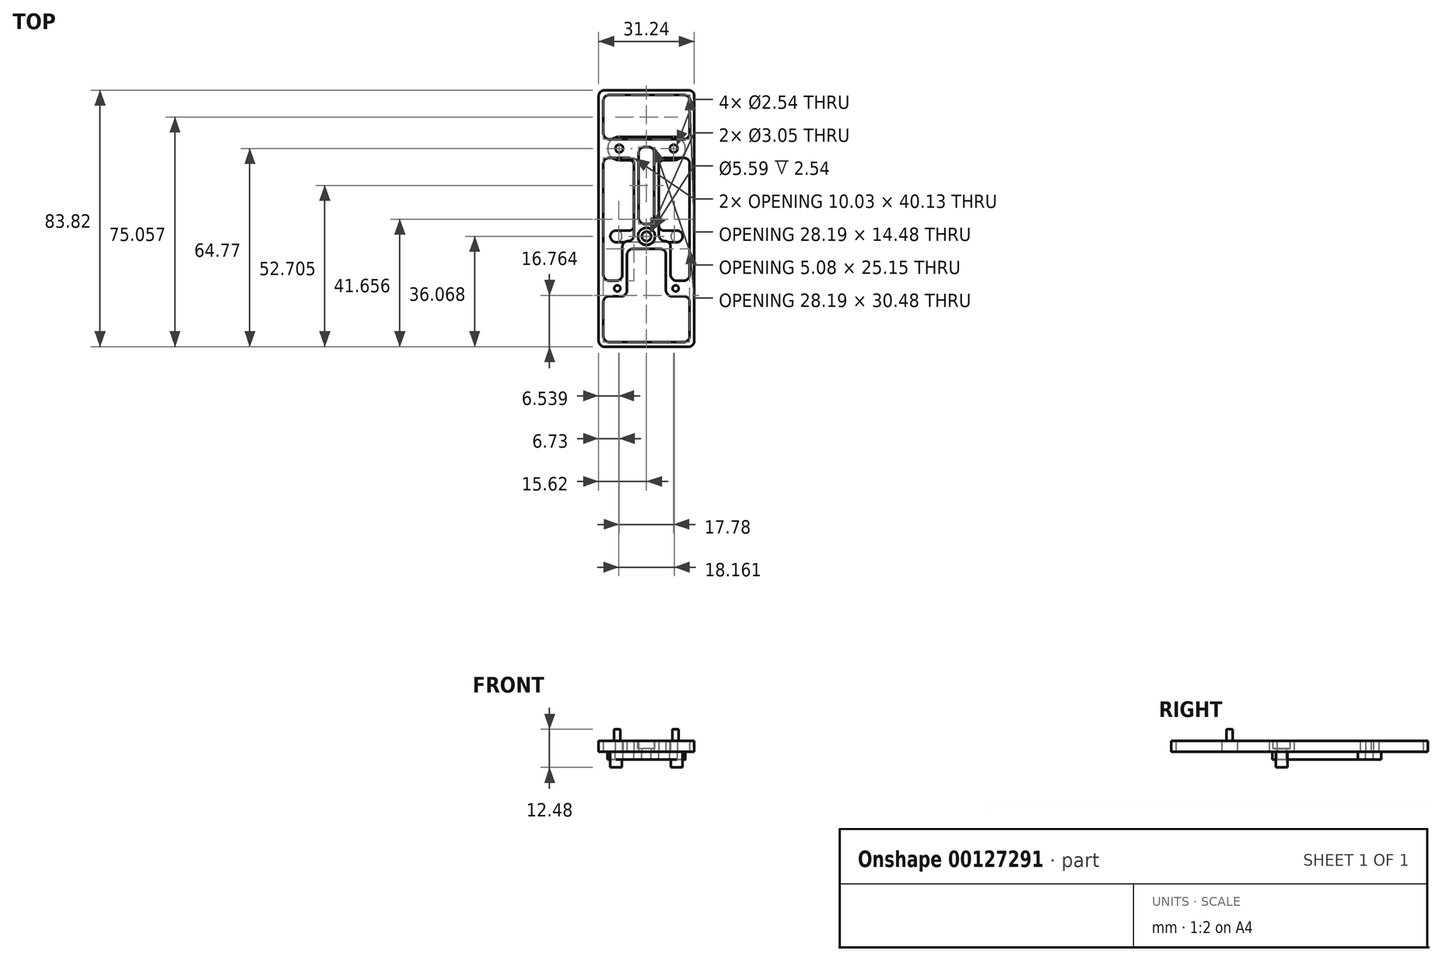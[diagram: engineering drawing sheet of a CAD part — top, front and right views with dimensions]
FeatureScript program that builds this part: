
annotation { "Feature Type Name" : "Feature", "Feature Type Description" : "" }
export const myFeature = defineFeature(function(context is Context, id is Id, definition is map)
    precondition{}
    {
        {
            var Q0;
            Q0=qCreatedBy(makeId("Top.planeOp"),FACE);
            var sketch = newSketch(context, id + "F0", { "sketchPlane" : qUnion([Q0])});
            skLineSegment(sketch, "E0.bottom", {"start": v(-15.62, 41.91) * mm, "end": v(15.62, 41.9) * mm});
            skLineSegment(sketch, "E0.top", {"start": v(-15.62, -41.91) * mm, "end": v(15.62, -41.91) * mm});
            skLineSegment(sketch, "E0.left", {"start": v(-15.62, 41.91) * mm, "end": v(-15.62, -41.91) * mm});
            skLineSegment(sketch, "E0.right", {"start": v(15.62, 41.91) * mm, "end": v(15.62, -41.91) * mm});
            skPoint(sketch, "E1", {"position": v(-15.62, 0) * mm});
            skPoint(sketch, "E2", {"position": v(0, 41.91) * mm});
            skLineSegment(sketch, "E3.bottom", {"start": v(-14.1, 40.39) * mm, "end": v(14.1, 40.39) * mm});
            skLineSegment(sketch, "E3.top", {"start": v(-14.1, -40.39) * mm, "end": v(14.1, -40.39) * mm});
            skLineSegment(sketch, "E3.left", {"start": v(-14.1, 40.39) * mm, "end": v(-14.1, 25.9) * mm});
            skLineSegment(sketch, "E3.right", {"start": v(14.1, 40.39) * mm, "end": v(14.1, 25.9) * mm});
            skPoint(sketch, "E4", {"position": v(0, 40.39) * mm});
            skPoint(sketch, "E5", {"position": v(-14.1, 0) * mm});
            skCircle(sketch, "E6", {"center": v(-8.9, 22.86) * mm, "radius": 1.27 * mm});
            skCircle(sketch, "E7", {"center": v(8.9, 22.86) * mm, "radius": 1.27 * mm});
            skCircle(sketch, "E8", {"center": v(9.53, -22.86) * mm, "radius": 1.02 * mm, "construction": true});
            skCircle(sketch, "E9", {"center": v(-9.53, -22.86) * mm, "radius": 1.02 * mm, "construction": true});
            skLineSegment(sketch, "E10", {"start": v(-8.9, 22.86) * mm, "end": v(-8.9, 19.81) * mm, "construction": true});
            skLineSegment(sketch, "E11", {"start": v(-9.53, -22.86) * mm, "end": v(9.53, -22.86) * mm, "construction": true});
            skLineSegment(sketch, "E12", {"start": v(-8.9, 22.86) * mm, "end": v(8.9, 22.86) * mm, "construction": true});
            skPoint(sketch, "E13", {"position": v(0, 22.86) * mm});
            skLineSegment(sketch, "E14", {"start": v(-14.1, 25.9) * mm, "end": v(-14.1, 19.81) * mm, "construction": true});
            skLineSegment(sketch, "E15", {"start": v(-14.1, 19.81) * mm, "end": v(-14.1, -20.32) * mm});
            skLineSegment(sketch, "E16", {"start": v(14.1, 25.9) * mm, "end": v(14.1, 19.81) * mm, "construction": true});
            skLineSegment(sketch, "E17", {"start": v(14.1, 19.81) * mm, "end": v(14.1, -20.32) * mm});
            skLineSegment(sketch, "E18", {"start": v(-14.1, 25.9) * mm, "end": v(14.1, 25.9) * mm});
            skLineSegment(sketch, "E19", {"start": v(-14.1, 19.81) * mm, "end": v(-4.06, 19.81) * mm});
            skLineSegment(sketch, "E20", {"start": v(-8.9, 22.86) * mm, "end": v(-8.9, 25.9) * mm, "construction": true});
            skCircle(sketch, "E21", {"center": v(0, -5.84) * mm, "radius": 1.52 * mm});
            skLineSegment(sketch, "E22", {"start": v(-4.06, 19.81) * mm, "end": v(-4.06, -7.37) * mm});
            skLineSegment(sketch, "E23", {"start": v(4.06, 19.81) * mm, "end": v(4.06, -7.37) * mm});
            skLineSegment(sketch, "E24", {"start": v(4.06, -7.37) * mm, "end": v(7.87, -7.37) * mm});
            skLineSegment(sketch, "E25", {"start": v(7.87, -7.37) * mm, "end": v(7.87, -20.32) * mm});
            skLineSegment(sketch, "E26", {"start": v(7.87, -20.32) * mm, "end": v(14.1, -20.32) * mm});
            skLineSegment(sketch, "E27", {"start": v(-4.06, -7.37) * mm, "end": v(-7.87, -7.37) * mm});
            skLineSegment(sketch, "E28", {"start": v(-7.87, -7.37) * mm, "end": v(-7.87, -20.32) * mm});
            skLineSegment(sketch, "E29", {"start": v(-7.87, -20.32) * mm, "end": v(-14.1, -20.32) * mm});
            skLineSegment(sketch, "E30", {"start": v(-4.06, -7.37) * mm, "end": v(4.06, -7.37) * mm, "construction": true});
            skPoint(sketch, "E31", {"position": v(0, -7.37) * mm});
            skLineSegment(sketch, "E32", {"start": v(-14.1, -25.4) * mm, "end": v(-6.35, -25.4) * mm});
            skLineSegment(sketch, "E33", {"start": v(-6.35, -25.4) * mm, "end": v(-6.35, -9.9) * mm});
            skLineSegment(sketch, "E34", {"start": v(-6.35, -9.9) * mm, "end": v(6.35, -9.9) * mm});
            skLineSegment(sketch, "E35", {"start": v(6.35, -9.9) * mm, "end": v(6.35, -25.4) * mm});
            skLineSegment(sketch, "E36", {"start": v(6.35, -25.4) * mm, "end": v(14.1, -25.4) * mm});
            skLineSegment(sketch, "E37", {"start": v(-14.1, -20.32) * mm, "end": v(-14.1, -25.4) * mm, "construction": true});
            skLineSegment(sketch, "E38", {"start": v(-14.1, -25.4) * mm, "end": v(-14.1, -40.39) * mm});
            skLineSegment(sketch, "E39", {"start": v(14.1, -25.4) * mm, "end": v(14.1, -40.39) * mm});
            skLineSegment(sketch, "E40", {"start": v(14.1, -20.32) * mm, "end": v(14.1, -25.4) * mm, "construction": true});
            skPoint(sketch, "E41", {"position": v(0, -9.9) * mm});
            skLineSegment(sketch, "E42", {"start": v(-4.06, 19.81) * mm, "end": v(4.06, 19.81) * mm, "construction": true});
            skLineSegment(sketch, "E43", {"start": v(4.06, 19.81) * mm, "end": v(14.1, 19.81) * mm});
            skLineSegment(sketch, "E44", {"start": v(-1.52, -5.84) * mm, "end": v(-4.06, -5.84) * mm, "construction": true});
            skLineSegment(sketch, "E45", {"start": v(-6.35, -9.9) * mm, "end": v(-6.35, -7.37) * mm, "construction": true});
            skPoint(sketch, "E46", {"position": v(-14.1, -22.86) * mm});
            skLineSegment(sketch, "E47", {"start": v(-9.53, -20.32) * mm, "end": v(-9.53, -22.86) * mm, "construction": true});
            skLineSegment(sketch, "E48", {"start": v(-9.53, -22.86) * mm, "end": v(-9.53, -25.4) * mm, "construction": true});
            skLineSegment(sketch, "E49.bottom", {"start": v(-2.54, 23.37) * mm, "end": v(2.54, 23.37) * mm});
            skLineSegment(sketch, "E49.top", {"start": v(-2.54, -1.78) * mm, "end": v(2.54, -1.78) * mm});
            skLineSegment(sketch, "E49.left", {"start": v(-2.54, 23.37) * mm, "end": v(-2.54, -1.78) * mm});
            skLineSegment(sketch, "E49.right", {"start": v(2.54, 23.37) * mm, "end": v(2.54, -1.78) * mm});
            skPoint(sketch, "E50", {"position": v(0, 23.37) * mm});
            skLineSegment(sketch, "E51", {"start": v(0, 23.37) * mm, "end": v(0, 25.9) * mm, "construction": true});
            skLineSegment(sketch, "E52", {"start": v(0, -1.78) * mm, "end": v(0, -4.32) * mm, "construction": true});
            skPoint(sketch, "E53", {"position": v(0, -22.86) * mm});
            skLineSegment(sketch, "E54", {"start": v(0, 22.86) * mm, "end": v(0, -22.86) * mm, "construction": true});
            skPoint(sketch, "E55", {"position": v(0, 0) * mm});
            skSolve(sketch);
        }
        {
            var Q0;
            Q0 = qSketchRegion(id + "F0", true);
            extrude(context, id + "F1", {"entities" : qUnion([Q0]), "depth" : 3.56 * mm});
        }
        {
            var Q0;
            Q0=makeQuery(id+"F1.opExtrude","SWEPT_EDGE",EDGE,{"disambiguationData":[OSD([sQuery(id+"F0.wireOp",EDGE,"E3.bottom"),sQuery(id+"F0.wireOp",EDGE,"E3.right")])]});
            var Q1;
            Q1=makeQuery(id+"F1.opExtrude","SWEPT_EDGE",EDGE,{"disambiguationData":[OSD([sQuery(id+"F0.wireOp",EDGE,"E3.bottom"),sQuery(id+"F0.wireOp",EDGE,"E3.left")])]});
            var Q2;
            Q2=makeQuery(id+"F1.opExtrude","SWEPT_EDGE",EDGE,{"disambiguationData":[OSD([sQuery(id+"F0.wireOp",EDGE,"E3.left"),sQuery(id+"F0.wireOp",EDGE,"E18")])]});
            var Q3;
            Q3=makeQuery(id+"F1.opExtrude","SWEPT_EDGE",EDGE,{"disambiguationData":[OSD([sQuery(id+"F0.wireOp",EDGE,"E3.right"),sQuery(id+"F0.wireOp",EDGE,"E18")])]});
            var Q4;
            Q4=makeQuery(id+"F1.opExtrude","SWEPT_EDGE",EDGE,{"disambiguationData":[OSD([sQuery(id+"F0.wireOp",EDGE,"E0.bottom"),sQuery(id+"F0.wireOp",EDGE,"E0.left")])]});
            var Q5;
            Q5=makeQuery(id+"F1.opExtrude","SWEPT_EDGE",EDGE,{"disambiguationData":[OSD([sQuery(id+"F0.wireOp",EDGE,"E0.bottom"),sQuery(id+"F0.wireOp",EDGE,"E0.right")])]});
            var Q6;
            Q6=makeQuery(id+"F1.opExtrude","SWEPT_EDGE",EDGE,{"disambiguationData":[OSD([sQuery(id+"F0.wireOp",EDGE,"E49.bottom"),sQuery(id+"F0.wireOp",EDGE,"E49.left")])]});
            var Q7;
            Q7=makeQuery(id+"F1.opExtrude","SWEPT_EDGE",EDGE,{"disambiguationData":[OSD([sQuery(id+"F0.wireOp",EDGE,"E15"),sQuery(id+"F0.wireOp",EDGE,"E19")])]});
            var Q8;
            Q8=makeQuery(id+"F1.opExtrude","SWEPT_EDGE",EDGE,{"disambiguationData":[OSD([sQuery(id+"F0.wireOp",EDGE,"E23"),sQuery(id+"F0.wireOp",EDGE,"E43")])]});
            var Q9;
            Q9=makeQuery(id+"F1.opExtrude","SWEPT_EDGE",EDGE,{"disambiguationData":[OSD([sQuery(id+"F0.wireOp",EDGE,"E19"),sQuery(id+"F0.wireOp",EDGE,"E22")])]});
            var Q10;
            Q10=makeQuery(id+"F1.opExtrude","SWEPT_EDGE",EDGE,{"disambiguationData":[OSD([sQuery(id+"F0.wireOp",EDGE,"E49.bottom"),sQuery(id+"F0.wireOp",EDGE,"E49.right")])]});
            var Q11;
            Q11=makeQuery(id+"F1.opExtrude","SWEPT_EDGE",EDGE,{"disambiguationData":[OSD([sQuery(id+"F0.wireOp",EDGE,"E17"),sQuery(id+"F0.wireOp",EDGE,"E43")])]});
            var Q12;
            Q12=makeQuery(id+"F1.opExtrude","SWEPT_EDGE",EDGE,{"disambiguationData":[OSD([sQuery(id+"F0.wireOp",EDGE,"E28"),sQuery(id+"F0.wireOp",EDGE,"E29")])]});
            var Q13;
            Q13=makeQuery(id+"F1.opExtrude","SWEPT_EDGE",EDGE,{"disambiguationData":[OSD([sQuery(id+"F0.wireOp",EDGE,"E27"),sQuery(id+"F0.wireOp",EDGE,"E28")])]});
            var Q14;
            Q14=makeQuery(id+"F1.opExtrude","SWEPT_EDGE",EDGE,{"disambiguationData":[OSD([sQuery(id+"F0.wireOp",EDGE,"E22"),sQuery(id+"F0.wireOp",EDGE,"E27")])]});
            var Q15;
            Q15=makeQuery(id+"F1.opExtrude","SWEPT_EDGE",EDGE,{"disambiguationData":[OSD([sQuery(id+"F0.wireOp",EDGE,"E49.top"),sQuery(id+"F0.wireOp",EDGE,"E49.right")])]});
            var Q16;
            Q16=makeQuery(id+"F1.opExtrude","SWEPT_EDGE",EDGE,{"disambiguationData":[OSD([sQuery(id+"F0.wireOp",EDGE,"E24"),sQuery(id+"F0.wireOp",EDGE,"E25")])]});
            var Q17;
            Q17=makeQuery(id+"F1.opExtrude","SWEPT_EDGE",EDGE,{"disambiguationData":[OSD([sQuery(id+"F0.wireOp",EDGE,"E17"),sQuery(id+"F0.wireOp",EDGE,"E26")])]});
            var Q18;
            Q18=makeQuery(id+"F1.opExtrude","SWEPT_EDGE",EDGE,{"disambiguationData":[OSD([sQuery(id+"F0.wireOp",EDGE,"E3.top"),sQuery(id+"F0.wireOp",EDGE,"E39")])]});
            var Q19;
            Q19=makeQuery(id+"F1.opExtrude","SWEPT_EDGE",EDGE,{"disambiguationData":[OSD([sQuery(id+"F0.wireOp",EDGE,"E35"),sQuery(id+"F0.wireOp",EDGE,"E36")])]});
            var Q20;
            Q20=makeQuery(id+"F1.opExtrude","SWEPT_EDGE",EDGE,{"disambiguationData":[OSD([sQuery(id+"F0.wireOp",EDGE,"E15"),sQuery(id+"F0.wireOp",EDGE,"E29")])]});
            var Q21;
            Q21=makeQuery(id+"F1.opExtrude","SWEPT_EDGE",EDGE,{"disambiguationData":[OSD([sQuery(id+"F0.wireOp",EDGE,"E25"),sQuery(id+"F0.wireOp",EDGE,"E26")])]});
            var Q22;
            Q22=makeQuery(id+"F1.opExtrude","SWEPT_EDGE",EDGE,{"disambiguationData":[OSD([sQuery(id+"F0.wireOp",EDGE,"E23"),sQuery(id+"F0.wireOp",EDGE,"E24")])]});
            var Q23;
            Q23=makeQuery(id+"F1.opExtrude","SWEPT_EDGE",EDGE,{"disambiguationData":[OSD([sQuery(id+"F0.wireOp",EDGE,"E49.top"),sQuery(id+"F0.wireOp",EDGE,"E49.left")])]});
            var Q24;
            Q24=makeQuery(id+"F1.opExtrude","SWEPT_EDGE",EDGE,{"disambiguationData":[OSD([sQuery(id+"F0.wireOp",EDGE,"E32"),sQuery(id+"F0.wireOp",EDGE,"E33")])]});
            var Q25;
            Q25=makeQuery(id+"F1.opExtrude","SWEPT_EDGE",EDGE,{"disambiguationData":[OSD([sQuery(id+"F0.wireOp",EDGE,"E3.top"),sQuery(id+"F0.wireOp",EDGE,"E38")])]});
            var Q26;
            Q26=makeQuery(id+"F1.opExtrude","SWEPT_EDGE",EDGE,{"disambiguationData":[OSD([sQuery(id+"F0.wireOp",EDGE,"E32"),sQuery(id+"F0.wireOp",EDGE,"E38")])]});
            var Q27;
            Q27=makeQuery(id+"F1.opExtrude","SWEPT_EDGE",EDGE,{"disambiguationData":[OSD([sQuery(id+"F0.wireOp",EDGE,"E33"),sQuery(id+"F0.wireOp",EDGE,"E34")])]});
            var Q28;
            Q28=makeQuery(id+"F1.opExtrude","SWEPT_EDGE",EDGE,{"disambiguationData":[OSD([sQuery(id+"F0.wireOp",EDGE,"E36"),sQuery(id+"F0.wireOp",EDGE,"E39")])]});
            var Q29;
            Q29=makeQuery(id+"F1.opExtrude","SWEPT_EDGE",EDGE,{"disambiguationData":[OSD([sQuery(id+"F0.wireOp",EDGE,"E34"),sQuery(id+"F0.wireOp",EDGE,"E35")])]});
            var Q30;
            Q30=makeQuery(id+"F1.opExtrude","SWEPT_EDGE",EDGE,{"disambiguationData":[OSD([sQuery(id+"F0.wireOp",EDGE,"E0.top"),sQuery(id+"F0.wireOp",EDGE,"E0.left")])]});
            var Q31;
            Q31=makeQuery(id+"F1.opExtrude","SWEPT_EDGE",EDGE,{"disambiguationData":[OSD([sQuery(id+"F0.wireOp",EDGE,"E0.top"),sQuery(id+"F0.wireOp",EDGE,"E0.right")])]});
            fillet(context, id + "F2", {"entities" : qUnion([Q0, Q1, Q2, Q3, Q4, Q5, Q6, Q7, Q8, Q9, Q10, Q11, Q12, Q13, Q14, Q15, Q16, Q17, Q18, Q19, Q20, Q21, Q22, Q23, Q24, Q25, Q26, Q27, Q28, Q29, Q30, Q31]), "radius" : 1.9 * mm, "tangentPropagation" : true, "allowEdgeOverflow" : false});
        }
        {
            var Q0;
            Q0=makeQuery(id+"F1.opExtrude","CAP_FACE",FACE,{"disambiguationData":[OSD([sQuery(id+"F0.wireOp",EDGE,"E0.bottom"),sQuery(id+"F0.wireOp",EDGE,"E0.top"),sQuery(id+"F0.wireOp",EDGE,"E0.left"),sQuery(id+"F0.wireOp",EDGE,"E0.right"),sQuery(id+"F0.wireOp",EDGE,"E3.bottom"),sQuery(id+"F0.wireOp",EDGE,"E3.top"),sQuery(id+"F0.wireOp",EDGE,"E3.left"),sQuery(id+"F0.wireOp",EDGE,"E3.right"),sQuery(id+"F0.wireOp",EDGE,"E6"),sQuery(id+"F0.wireOp",EDGE,"E7"),sQuery(id+"F0.wireOp",EDGE,"E15"),sQuery(id+"F0.wireOp",EDGE,"E17"),sQuery(id+"F0.wireOp",EDGE,"E18"),sQuery(id+"F0.wireOp",EDGE,"E19"),sQuery(id+"F0.wireOp",EDGE,"E21"),sQuery(id+"F0.wireOp",EDGE,"E22"),sQuery(id+"F0.wireOp",EDGE,"E23"),sQuery(id+"F0.wireOp",EDGE,"E24"),sQuery(id+"F0.wireOp",EDGE,"E25"),sQuery(id+"F0.wireOp",EDGE,"E26"),sQuery(id+"F0.wireOp",EDGE,"E27"),sQuery(id+"F0.wireOp",EDGE,"E28"),sQuery(id+"F0.wireOp",EDGE,"E29"),sQuery(id+"F0.wireOp",EDGE,"E32"),sQuery(id+"F0.wireOp",EDGE,"E33"),sQuery(id+"F0.wireOp",EDGE,"E34"),sQuery(id+"F0.wireOp",EDGE,"E35"),sQuery(id+"F0.wireOp",EDGE,"E36"),sQuery(id+"F0.wireOp",EDGE,"E38"),sQuery(id+"F0.wireOp",EDGE,"E39"),sQuery(id+"F0.wireOp",EDGE,"E43"),sQuery(id+"F0.wireOp",EDGE,"E49.bottom"),sQuery(id+"F0.wireOp",EDGE,"E49.top"),sQuery(id+"F0.wireOp",EDGE,"E49.left"),sQuery(id+"F0.wireOp",EDGE,"E49.right")])],"isStart":false});
            var sketch = newSketch(context, id + "F3", { "sketchPlane" : qUnion([Q0])});
            skCircle(sketch, "E56", {"center": v(-9.53, -22.86) * mm, "radius": 1.02 * mm});
            skCircle(sketch, "E57", {"center": v(9.53, -22.86) * mm, "radius": 1.02 * mm});
            skSolve(sketch);
        }
        {
            var Q0;
            Q0 = qSketchRegion(id + "F3", true);
            extrude(context, id + "F4", {"entities" : qUnion([Q0]), "operationType" : NewBodyOperationType.ADD, "depth" : 3.8 * mm});
        }
        {
            var Q0;
            Q0=makeQuery(id+"F1.opExtrude","CAP_FACE",FACE,{"disambiguationData":[OSD([sQuery(id+"F0.wireOp",EDGE,"E0.bottom"),sQuery(id+"F0.wireOp",EDGE,"E0.top"),sQuery(id+"F0.wireOp",EDGE,"E0.left"),sQuery(id+"F0.wireOp",EDGE,"E0.right"),sQuery(id+"F0.wireOp",EDGE,"E3.bottom"),sQuery(id+"F0.wireOp",EDGE,"E3.top"),sQuery(id+"F0.wireOp",EDGE,"E3.left"),sQuery(id+"F0.wireOp",EDGE,"E3.right"),sQuery(id+"F0.wireOp",EDGE,"E6"),sQuery(id+"F0.wireOp",EDGE,"E7"),sQuery(id+"F0.wireOp",EDGE,"E15"),sQuery(id+"F0.wireOp",EDGE,"E17"),sQuery(id+"F0.wireOp",EDGE,"E18"),sQuery(id+"F0.wireOp",EDGE,"E19"),sQuery(id+"F0.wireOp",EDGE,"E21"),sQuery(id+"F0.wireOp",EDGE,"E22"),sQuery(id+"F0.wireOp",EDGE,"E23"),sQuery(id+"F0.wireOp",EDGE,"E24"),sQuery(id+"F0.wireOp",EDGE,"E25"),sQuery(id+"F0.wireOp",EDGE,"E26"),sQuery(id+"F0.wireOp",EDGE,"E27"),sQuery(id+"F0.wireOp",EDGE,"E28"),sQuery(id+"F0.wireOp",EDGE,"E29"),sQuery(id+"F0.wireOp",EDGE,"E32"),sQuery(id+"F0.wireOp",EDGE,"E33"),sQuery(id+"F0.wireOp",EDGE,"E34"),sQuery(id+"F0.wireOp",EDGE,"E35"),sQuery(id+"F0.wireOp",EDGE,"E36"),sQuery(id+"F0.wireOp",EDGE,"E38"),sQuery(id+"F0.wireOp",EDGE,"E39"),sQuery(id+"F0.wireOp",EDGE,"E43"),sQuery(id+"F0.wireOp",EDGE,"E49.bottom"),sQuery(id+"F0.wireOp",EDGE,"E49.top"),sQuery(id+"F0.wireOp",EDGE,"E49.left"),sQuery(id+"F0.wireOp",EDGE,"E49.right")])],"isStart":false});
            var sketch = newSketch(context, id + "F5", { "sketchPlane" : qUnion([Q0])});
            skCircle(sketch, "E58", {"center": v(0, -5.84) * mm, "radius": 2.8 * mm});
            skSolve(sketch);
        }
        {
            var Q0;
            Q0 = qSketchRegion(id + "F5", true);
            extrude(context, id + "F6", {"entities" : qUnion([Q0]), "operationType" : NewBodyOperationType.REMOVE, "oppositeDirection" : true, "depth" : 2.54 * mm});
        }
        {
            var Q0;
            Q0=qCreatedBy(makeId("Top.planeOp"),FACE);
            cPlane(context, id + "F7", {"entities" : qUnion([Q0]), "cplaneType" : CPlaneType.OFFSET, "offset" : 0.03 * mm, "oppositeDirection" : true, "width" : 152.4 * mm, "height" : 152.4 * mm});
        }
        {
            var Q0;
            Q0=qCreatedBy(id+"F7.planeOp",FACE);
            var sketch = newSketch(context, id + "F8", { "sketchPlane" : qUnion([Q0])});
            skCircle(sketch, "E59", {"center": v(9.9, -5.84) * mm, "radius": 1.9 * mm, "construction": true});
            skCircle(sketch, "E60", {"center": v(-9.9, -5.84) * mm, "radius": 1.9 * mm, "construction": true});
            skLineSegment(sketch, "E61", {"start": v(8, -5.84) * mm, "end": v(-8, -5.84) * mm, "construction": true});
            skPoint(sketch, "E62", {"position": v(0, -5.84) * mm});
            skLineSegment(sketch, "E63", {"start": v(9.9, -7.75) * mm, "end": v(2.38, -7.75) * mm});
            skLineSegment(sketch, "E64", {"start": v(-9.9, -3.94) * mm, "end": v(-4.06, -3.94) * mm});
            skLineSegment(sketch, "E65", {"start": v(9.9, -3.94) * mm, "end": v(4.06, -3.94) * mm});
            skArc(sketch, "E66", {"start": v(9.9, -7.75) * mm, "mid": v(11.81, -5.84) * mm, "end": v(9.9, -3.94) * mm});
            skArc(sketch, "E67", {"start": v(-9.9, -3.94) * mm, "mid": v(-11.81, -5.84) * mm, "end": v(-9.9, -7.75) * mm});
            skCircle(sketch, "E68", {"center": v(0, -5.84) * mm, "radius": 1.52 * mm});
            skLineSegment(sketch, "E69", {"start": v(2.38, -7.75) * mm, "end": v(-2.38, -7.75) * mm, "construction": true});
            skLineSegment(sketch, "E70", {"start": v(-2.38, -7.75) * mm, "end": v(-9.9, -7.75) * mm});
            skArc(sketch, "E71", {"start": v(-2.38, -7.75) * mm, "mid": v(0, -8.89) * mm, "end": v(2.38, -7.75) * mm});
            skCircle(sketch, "E72", {"center": v(8.9, 22.86) * mm, "radius": 1.27 * mm});
            skCircle(sketch, "E73", {"center": v(-8.9, 22.86) * mm, "radius": 1.27 * mm});
            skLineSegment(sketch, "E74", {"start": v(8.9, 26.67) * mm, "end": v(-8.9, 26.67) * mm});
            skLineSegment(sketch, "E75", {"start": v(8.9, 26.67) * mm, "end": v(8.9, 24.13) * mm, "construction": true});
            skLineSegment(sketch, "E76", {"start": v(4.06, -3.94) * mm, "end": v(4.06, 19.05) * mm});
            skLineSegment(sketch, "E77", {"start": v(4.06, 19.05) * mm, "end": v(8.9, 19.05) * mm});
            skLineSegment(sketch, "E78", {"start": v(-4.06, -3.94) * mm, "end": v(-4.06, 19.05) * mm});
            skLineSegment(sketch, "E79", {"start": v(-4.06, 19.05) * mm, "end": v(-8.9, 19.05) * mm});
            skArc(sketch, "E80", {"start": v(8.9, 19.05) * mm, "mid": v(12.7, 22.86) * mm, "end": v(8.9, 26.67) * mm});
            skArc(sketch, "E81", {"start": v(-8.9, 26.67) * mm, "mid": v(-12.7, 22.86) * mm, "end": v(-8.9, 19.05) * mm});
            skSolve(sketch);
        }
        {
            var Q0;
            Q0 = qSketchRegion(id + "F8", true);
            extrude(context, id + "F9", {"entities" : qUnion([Q0]), "oppositeDirection" : true, "depth" : 2.54 * mm});
        }
        {
            var Q0;
            Q0=makeQuery(id+"F9.opExtrude","SWEPT_EDGE",EDGE,{"disambiguationData":[OSD([sQuery(id+"F8.wireOp",EDGE,"E64"),sQuery(id+"F8.wireOp",EDGE,"BaYNkTW9-8C4l-3Pi0-YyGr-iQm0XArgOPPM")])]});
            var Q1;
            Q1=makeQuery(id+"F9.opExtrude","SWEPT_EDGE",EDGE,{"disambiguationData":[OSD([sQuery(id+"F8.wireOp",EDGE,"E65"),sQuery(id+"F8.wireOp",EDGE,"39ISVxld-jYe8-9ziI-GPcq-S6yEnfoZS8ja")])]});
            var Q2;
            Q2=makeQuery(id+"F9.opExtrude","SWEPT_EDGE",EDGE,{"disambiguationData":[OSD([sQuery(id+"F8.wireOp",EDGE,"E63"),sQuery(id+"F8.wireOp",EDGE,"E71")])]});
            var Q3;
            Q3=makeQuery(id+"F9.opExtrude","SWEPT_EDGE",EDGE,{"disambiguationData":[OSD([sQuery(id+"F8.wireOp",EDGE,"E70"),sQuery(id+"F8.wireOp",EDGE,"E71")])]});
            var Q4;
            Q4=makeQuery(id+"F9.opExtrude","SWEPT_EDGE",EDGE,{"disambiguationData":[OSD([sQuery(id+"F8.wireOp",EDGE,"E78"),sQuery(id+"F8.wireOp",EDGE,"E79")])]});
            var Q5;
            Q5=makeQuery(id+"F9.opExtrude","SWEPT_EDGE",EDGE,{"disambiguationData":[OSD([sQuery(id+"F8.wireOp",EDGE,"E76"),sQuery(id+"F8.wireOp",EDGE,"E77")])]});
            fillet(context, id + "F10", {"entities" : qUnion([Q0, Q1, Q2, Q3, Q4, Q5]), "radius" : 1.52 * mm, "tangentPropagation" : true, "allowEdgeOverflow" : false});
        }
        {
            var Q0;
            Q0=makeQuery(id+"F9.opExtrude","CAP_FACE",FACE,{"disambiguationData":[OSD([sQuery(id+"F8.wireOp",EDGE,"ZwspYAmu-Z6Zr-nvel-RZDx-r3O5OsN73eEC"),sQuery(id+"F8.wireOp",EDGE,"E63"),sQuery(id+"F8.wireOp",EDGE,"E64"),sQuery(id+"F8.wireOp",EDGE,"BaYNkTW9-8C4l-3Pi0-YyGr-iQm0XArgOPPM"),sQuery(id+"F8.wireOp",EDGE,"E65"),sQuery(id+"F8.wireOp",EDGE,"39ISVxld-jYe8-9ziI-GPcq-S6yEnfoZS8ja"),sQuery(id+"F8.wireOp",EDGE,"AimVFt3a-mOmf-XyMT-WdKR-8qlM9l11iZe7"),sQuery(id+"F8.wireOp",EDGE,"E66"),sQuery(id+"F8.wireOp",EDGE,"E67"),sQuery(id+"F8.wireOp",EDGE,"E68"),sQuery(id+"F8.wireOp",EDGE,"E70"),sQuery(id+"F8.wireOp",EDGE,"E71")])],"isStart":false});
            var sketch = newSketch(context, id + "F11", { "sketchPlane" : qUnion([Q0])});
            skCircle(sketch, "E82", {"center": v(9.9, 5.84) * mm, "radius": 1.9 * mm});
            skCircle(sketch, "E83", {"center": v(-9.9, 5.84) * mm, "radius": 1.9 * mm});
            skSolve(sketch);
        }
        {
            var Q0;
            Q0 = qSketchRegion(id + "F11", true);
            extrude(context, id + "F12", {"entities" : qUnion([Q0]), "operationType" : NewBodyOperationType.ADD, "depth" : 2.54 * mm});
        }
    });
